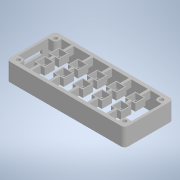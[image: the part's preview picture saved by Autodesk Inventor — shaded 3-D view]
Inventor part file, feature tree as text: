
AUTODESK INVENTOR PART (.ipt)
format: ipt  version: 2022.1 (Build 261234020, 234B)  size: 386,560 bytes
history: native  units: in
note: dims shown in document units (in); Inventor stores cm internally (conversion verified against a paired STEP export)
features: other x4, sketch x3, extrude x2
ambient origin geometry x8: Origin, YZ Plane, XZ Plane, XY Plane, X Axis, Y Axis, Z Axis, Center Point
bodies: Solido1 (feature_tree), Body1 (feature_tree)
feature tree (9):
  other  "Geometria corretta1"
  other  "Ispessimento1"
  other  "Ispessimento2"
  extrude  "Estrusione1"  Depth=0.126in
  sketch  "Schizzo4"
  extrude  "Estrusione2"  Depth=0.126in
  sketch  "Schizzo3"
  other  "Linea chiusa proiettata1"
  sketch  "Schizzo5"
